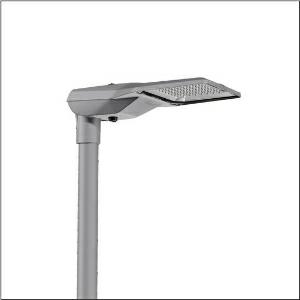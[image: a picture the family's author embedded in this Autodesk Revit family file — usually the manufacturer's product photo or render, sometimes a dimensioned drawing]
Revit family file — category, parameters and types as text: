
# Revit family: streetlight_sl_21_iq_midi___pc-l_5xe3f31y08mb_244c
name_source: partatom
category: Lighting Fixtures
units: mm (PartAtom-declared; Revit-internal decimal feet)

## family parameters
Cut with Voids When Loaded = No
Host = Face
Light Source = No
Part Type = Normal
Room Calculation Point = No
Round Connector Dimension = Use Diameter
Shared = No

## types (1)
- --- (1 x LED, 17070 lm, 129.3 W, 3000K)
    Apparent Load = 129 VA
    CIE Flux Codes = 38 78 98 100 100
    Color Rendering = 70
    Color Temperature = 3000K
    Default Elevation = 1800 mm
    Description = Streetlight SL 21 iQ midi, mast luminaire, primary light control with lens, of PMMA, primary optical cover: cover, of toughened safety glass, transparent, light distribution: PC-L, light emission: direct distribution, primary light characteristic: asymmetric, left, installation type: post-top, side-entry, LED, High Power LED, rated luminous flux: 17.070lm, luminous efficacy: 132lm/W, light colour: 730, colour temperature: 3000K, control gear: iQ-Street Remote, D4i with power reduction, control: pre-setting: logarithmic dimming characteristic, Street-Remote, Auto-Match, Temp-Guard, Lumen-Switch, Night-Set, Smart-Wire, Light-Fading, Desk-Remote (wireless, voltage-free reading and setting of iQ features in the workshop via application-optimized NFC function/RFID function), optimised constant luminous flux control (CLO 2.0), mains connection: 230..240V, AC, 50/60Hz, start of lifetime: 129W, end of service life: 142W, reduction: 56W, luminaire housing, of diecast aluminium, powder-coated, SITECO metallic grey (DB 702S), corrosivity category C5 high according to DIN EN ISO 12944, please order mast flange separately, inclination adjustable: 0°, 5°, 10°, 15°, sealing non-destructively replaceable, multi-level sealing system, length: 644mm, width: 335mm, height: 110mm, mast flange for spigot size: 42mm (side-entry): 5XC10008XM4, 60/48mm (side-entry/post-top): 5XC10108XM2, 76/60mm (side-entry/post-top): 5XC10108XM1, mounting height: 4..8m, Smart Interface below and above, protection rating (complete): IP66, insulation class (complete): insulation class II (safety insulation), certification: CE, ENEC, ENEC+, VDE, impact resistance: IK10, permissible operating ambient temperature for outdoor applications: -40..+50°C, standard-compliant lighting for roads and squares, packaging unit: 1 piece

Light Distribution: PC-L
    Height = 111 mm
    Lamp = 1 x LED
    Lamp Light Flux = 17070 lm
    Lamp Power = 129.3 W
    Lamp count = 1
    Length = 644 mm
    Luminous efficacy = 132 lm/W
    Manufacturer = Siteco
    ModVariant = No
    Model = 5XE3F31Y08MB
    Number of Poles = 1
    OnlyDefault = Yes
    Power Factor = 1
    Product Name = Streetlight SL 21 iQ midi | PC-L
    Product group = mast luminaire | pylon top
    ProductGroupID = 6100
    Protection Class = Protection class II
    Protection Degree = IP 66
    RLX_Detail_Level = 1
    RLX_Emergency_Light_Flux = 0 lm
    RLX_Emergency_Type = 0
    RLX_Emergency_Type_DB = No
    RlxData = <blob elided: 29841 chars, md5=55cce668>
    Socket = socket
    Standby Power = 0 W
    System Light Flux = 17070 lm
    System Power = 129 W
    Type Comments = factory setting: luminous flux: 100 % | dim-lin: 254 | 672 mA
    Type Image = l_1004304.jpg
    URL = http://relux.com
    VarID = @adj_072231
    Voltage = 0 V
    Weight = 0.00 kg
    Width = 336 mm

## geometry (parser evidence)
native form markers: Blend x4, Sweep x11
no freeform markers — native parametric forms only
